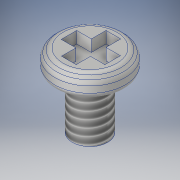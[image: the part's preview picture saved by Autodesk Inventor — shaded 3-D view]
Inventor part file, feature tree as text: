
AUTODESK INVENTOR PART (.ipt)
format: ipt  version: 2018 (Build 220112000, 112)  size: 171,520 bytes
history: native  units: in
note: dims shown in document units (in); Inventor stores cm internally (conversion verified against a paired STEP export)
features: sketch x2, revolve x1, chamfer x1, fillet x1, thread x1, extrude x1
ambient origin geometry x8: Origin, YZ Plane, XZ Plane, XY Plane, X Axis, Y Axis, Z Axis, Center Point
bodies: Solid1 (feature_tree)
feature tree (7):
  revolve  "Revolution1"  [1 undecoded]
  chamfer  "Chamfer1"  Distance=0.225in
  fillet  "Fillet1"  [1 undecoded]
  thread  "Thread1"  [1 undecoded]
  extrude  "Extrusion1"  Depth=0.025in TaperAngle=45.0deg
  sketch  "Sketch1"  dims[d0=0.15in d1=0.0875in]
  sketch  "Sketch2"  dims[d2=0.075in d3=0.225in d4=90.0deg d5=90.0deg d6=0.025in d7=0.125in d8=45.0deg d9=0.025in d10=1.0in d11=0.0in d12=0.05in d13=0.0in]
note: 3 required parameter values undecoded (feature->parameter linkage not recoverable at this tier; creation-order binding heuristic only, values carry confidence <= 0.55)